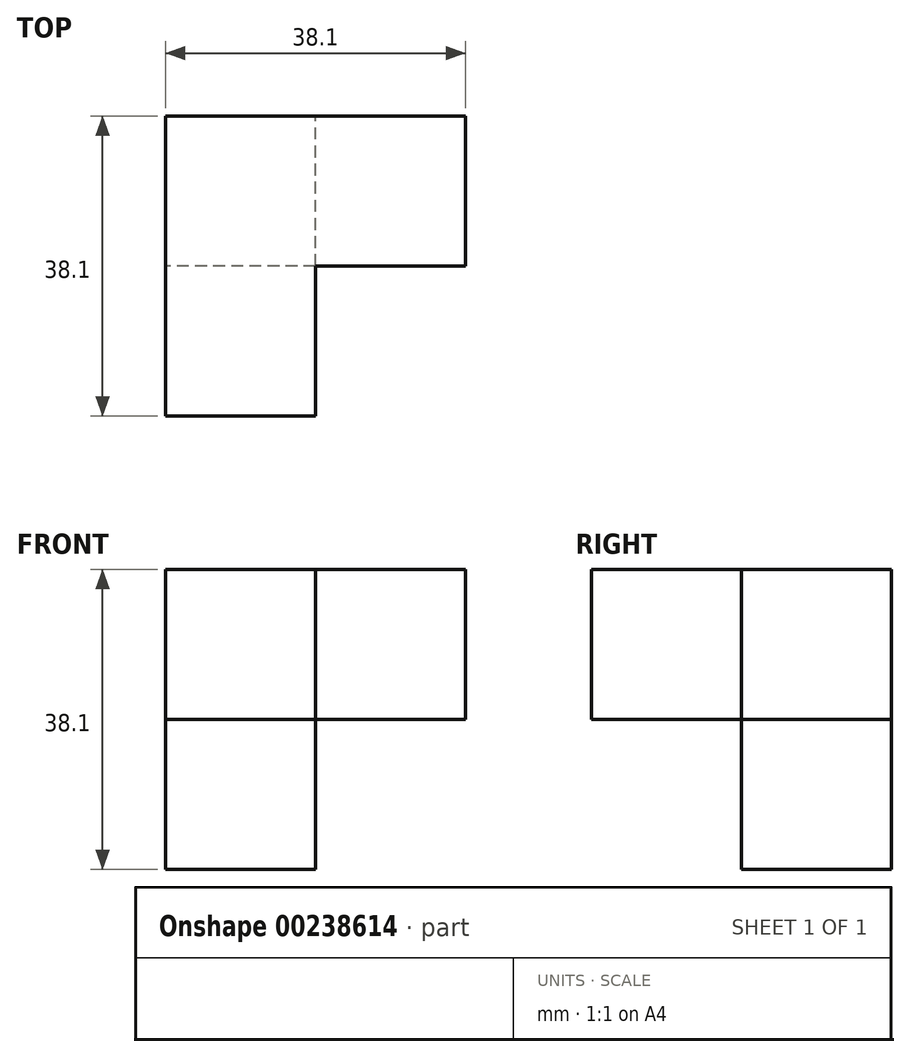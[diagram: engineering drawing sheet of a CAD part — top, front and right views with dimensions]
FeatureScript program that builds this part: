
annotation { "Feature Type Name" : "Feature", "Feature Type Description" : "" }
export const myFeature = defineFeature(function(context is Context, id is Id, definition is map)
    precondition{}
    {
        {
            var Q0;
            Q0=qCreatedBy(makeId("Top.planeOp"),FACE);
            var sketch = newSketch(context, id + "F0", { "sketchPlane" : qUnion([Q0])});
            skLineSegment(sketch, "E0", {"start": v(0, 0) * mm, "end": v(38.1, 0) * mm});
            skLineSegment(sketch, "E1", {"start": v(38.1, 0) * mm, "end": v(38.1, -19.05) * mm});
            skLineSegment(sketch, "E2", {"start": v(38.1, -19.05) * mm, "end": v(19.05, -19.05) * mm});
            skLineSegment(sketch, "E3", {"start": v(19.05, -19.05) * mm, "end": v(19.05, -38.1) * mm});
            skLineSegment(sketch, "E4", {"start": v(19.05, -38.1) * mm, "end": v(0, -38.1) * mm});
            skLineSegment(sketch, "E5", {"start": v(0, -38.1) * mm, "end": v(0, 0) * mm});
            skSolve(sketch);
        }
        {
            var Q0;
            Q0 = qSketchRegion(id + "F0", true);
            extrude(context, id + "F1", {"entities" : qUnion([Q0]), "depth" : 19.05 * mm});
        }
        {
            var Q0;
            Q0=makeQuery(id+"F1.opExtrude","CAP_FACE",FACE,{"disambiguationData":[OSD([sQuery(id+"F0.wireOp",EDGE,"E0"),sQuery(id+"F0.wireOp",EDGE,"E1"),sQuery(id+"F0.wireOp",EDGE,"E2"),sQuery(id+"F0.wireOp",EDGE,"E3"),sQuery(id+"F0.wireOp",EDGE,"E4"),sQuery(id+"F0.wireOp",EDGE,"E5")])],"isStart":true});
            var sketch = newSketch(context, id + "F2", { "sketchPlane" : qUnion([Q0])});
            skLineSegment(sketch, "E6.bottom", {"start": v(19.05, 19.05) * mm, "end": v(0, 19.05) * mm});
            skLineSegment(sketch, "E6.top", {"start": v(19.05, 0) * mm, "end": v(0, 0) * mm});
            skLineSegment(sketch, "E6.left", {"start": v(19.05, 19.05) * mm, "end": v(19.05, 0) * mm});
            skLineSegment(sketch, "E6.right", {"start": v(0, 19.05) * mm, "end": v(0, 0) * mm});
            skSolve(sketch);
        }
        {
            var Q0;
            Q0 = qSketchRegion(id + "F2", true);
            extrude(context, id + "F3", {"entities" : qUnion([Q0]), "operationType" : NewBodyOperationType.ADD, "depth" : 19.05 * mm});
        }
    });
